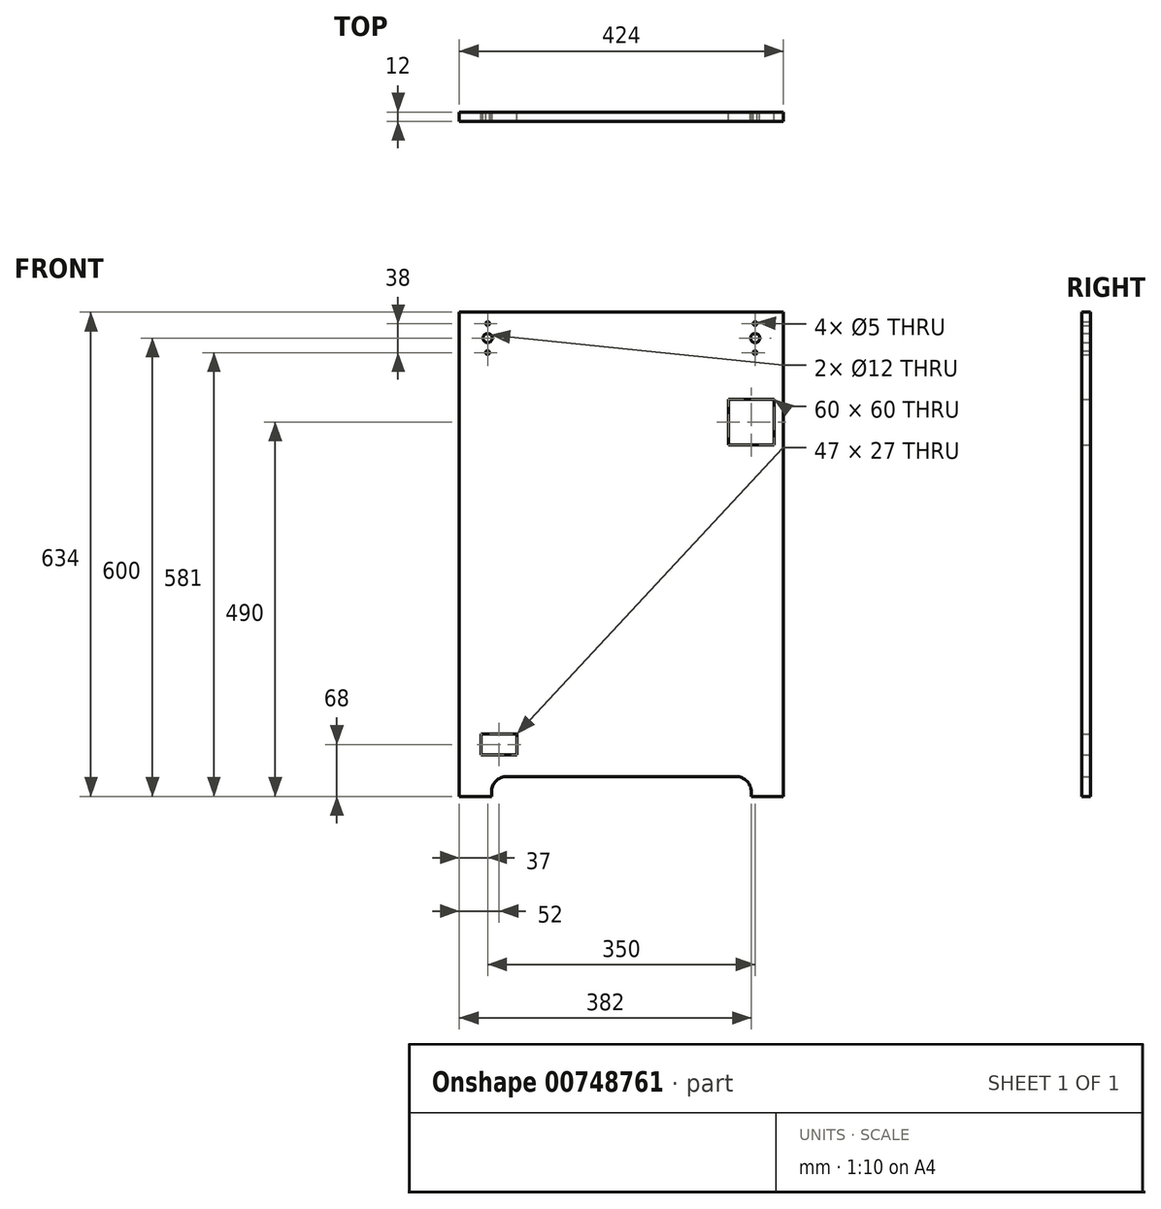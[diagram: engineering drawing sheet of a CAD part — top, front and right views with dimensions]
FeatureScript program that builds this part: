
annotation { "Feature Type Name" : "Feature", "Feature Type Description" : "" }
export const myFeature = defineFeature(function(context is Context, id is Id, definition is map)
    precondition{}
    {
        {
            assignVariable(context, id + "F0", {"name" : "Width", "anyValue" : 12});
        }
        {
            var Q0;
            Q0=qCreatedBy(makeId("Front.planeOp"),FACE);
            var sketch = newSketch(context, id + "F1", { "sketchPlane" : qUnion([Q0])});
            skLineSegment(sketch, "E0.bottom", {"start": v(200, 374) * mm, "end": v(-200, 374) * mm});
            skLineSegment(sketch, "E0.top", {"start": v(200, -260) * mm, "end": v(-200, -260) * mm});
            skLineSegment(sketch, "E0.left", {"start": v(200, 374) * mm, "end": v(200, -260) * mm});
            skLineSegment(sketch, "E0.right", {"start": v(-200, 374) * mm, "end": v(-200, -260) * mm});
            skPoint(sketch, "E1.middle", {"position": v(0, 0) * mm});
            skCircle(sketch, "E2", {"center": v(175, 340) * mm, "radius": 6 * mm});
            skCircle(sketch, "E3", {"center": v(-175, 340) * mm, "radius": 6 * mm});
            skLineSegment(sketch, "E4", {"start": v(200, -150) * mm, "end": v(-200, -150) * mm});
            skLineSegment(sketch, "E5", {"start": v(-200, -150) * mm, "end": v(-200, -162) * mm});
            skLineSegment(sketch, "E6", {"start": v(-200, -162) * mm, "end": v(200, -162) * mm});
            skLineSegment(sketch, "E7", {"start": v(200, -162) * mm, "end": v(200, -150) * mm});
            skLineSegment(sketch, "E8", {"start": v(-200, -260) * mm, "end": v(-212, -260) * mm});
            skLineSegment(sketch, "E9", {"start": v(-212, -260) * mm, "end": v(-212, 374) * mm});
            skLineSegment(sketch, "E10", {"start": v(-212, 374) * mm, "end": v(-200, 374) * mm});
            skLineSegment(sketch, "E11", {"start": v(200, 374) * mm, "end": v(212, 374) * mm});
            skLineSegment(sketch, "E12", {"start": v(212, 374) * mm, "end": v(212, -260) * mm});
            skLineSegment(sketch, "E13", {"start": v(212, -260) * mm, "end": v(200, -260) * mm});
            skLineSegment(sketch, "E14", {"start": v(-200, -222) * mm, "end": v(200, -222) * mm});
            skLineSegment(sketch, "E15", {"start": v(200, -222) * mm, "end": v(200, -234) * mm});
            skLineSegment(sketch, "E16", {"start": v(-200, -234) * mm, "end": v(-200, -222) * mm});
            skLineSegment(sketch, "E17", {"start": v(-170, -254) * mm, "end": v(-170, -260) * mm});
            skLineSegment(sketch, "E18", {"start": v(170, -254) * mm, "end": v(170, -260) * mm});
            skLineSegment(sketch, "E19", {"start": v(-150, -234) * mm, "end": v(150, -234) * mm});
            skArc(sketch, "E20.filletArc", {"start": v(170, -254) * mm, "mid": v(164.14, -239.86) * mm, "end": v(150, -234) * mm});
            skArc(sketch, "E21.filletArc", {"start": v(-150, -234) * mm, "mid": v(-164.14, -239.86) * mm, "end": v(-170, -254) * mm});
            skLineSegment(sketch, "E22", {"start": v(-200, -234) * mm, "end": v(-150, -234) * mm});
            skLineSegment(sketch, "E23", {"start": v(150, -234) * mm, "end": v(200, -234) * mm});
            skCircle(sketch, "E24", {"center": v(-175, 359) * mm, "radius": 2.5 * mm});
            skCircle(sketch, "E25", {"center": v(-175, 321) * mm, "radius": 2.5 * mm});
            skCircle(sketch, "E26", {"center": v(175, 359) * mm, "radius": 2.5 * mm});
            skCircle(sketch, "E27", {"center": v(175, 321) * mm, "radius": 2.5 * mm});
            skLineSegment(sketch, "E28.bottom", {"start": v(200, 200) * mm, "end": v(140, 200) * mm});
            skLineSegment(sketch, "E28.top", {"start": v(200, 260) * mm, "end": v(140, 260) * mm});
            skLineSegment(sketch, "E28.left", {"start": v(200, 200) * mm, "end": v(200, 260) * mm});
            skLineSegment(sketch, "E28.right", {"start": v(140, 200) * mm, "end": v(140, 260) * mm});
            skPoint(sketch, "E28.middle", {"position": v(170, 230) * mm});
            skLineSegment(sketch, "E29.bottom", {"start": v(-136.5, -178.5) * mm, "end": v(-183.5, -178.5) * mm});
            skLineSegment(sketch, "E29.top", {"start": v(-136.5, -205.5) * mm, "end": v(-183.5, -205.5) * mm});
            skLineSegment(sketch, "E29.left", {"start": v(-136.5, -178.5) * mm, "end": v(-136.5, -205.5) * mm});
            skLineSegment(sketch, "E29.right", {"start": v(-183.5, -178.5) * mm, "end": v(-183.5, -205.5) * mm});
            skSolve(sketch);
        }
        {
            var Q0;
            {var subQ1=sQuery(id+"F1.wireOp",EDGE,"E0.bottom");Q0=makeQuery(id+"F1.imprint","IMPRINT",FACE,{"disambiguationData":[TD([[makeQuery(id+"F1.imprint","IMPRINT",EDGE,{"derivedFrom":subQ1}),1.0]])]});}
            var Q1;
            {var subQ5=sQuery(id+"F1.wireOp",EDGE,"E11");Q1=makeQuery(id+"F1.imprint","IMPRINT",FACE,{"disambiguationData":[TD([[makeQuery(id+"F1.imprint","IMPRINT",EDGE,{"derivedFrom":subQ5}),-1.0]])]});}
            var Q2;
            {var subQ3=sQuery(id+"F1.wireOp",EDGE,"E8");Q2=makeQuery(id+"F1.imprint","IMPRINT",FACE,{"disambiguationData":[TD([[makeQuery(id+"F1.imprint","IMPRINT",EDGE,{"derivedFrom":subQ3}),-1.0]])]});}
            var Q3;
            {var subQ2=sQuery(id+"F1.wireOp",EDGE,"E4");Q3=makeQuery(id+"F1.imprint","IMPRINT",FACE,{"disambiguationData":[TD([[makeQuery(id+"F1.imprint","IMPRINT",EDGE,{"derivedFrom":subQ2}),1.0]])]});}
            var Q4;
            {var subQ1=sQuery(id+"F1.wireOp",EDGE,"E6");Q4=makeQuery(id+"F1.imprint","IMPRINT",FACE,{"disambiguationData":[TD([[makeQuery(id+"F1.imprint","IMPRINT",EDGE,{"derivedFrom":subQ1}),-1.0]])]});}
            var Q5;
            {var subQ0=sQuery(id+"F1.wireOp",EDGE,"E14");Q5=makeQuery(id+"F1.imprint","IMPRINT",FACE,{"disambiguationData":[TD([[makeQuery(id+"F1.imprint","IMPRINT",EDGE,{"derivedFrom":subQ0}),-1.0]])]});}
            var Q6;
            {var subQ0=sQuery(id+"F1.wireOp",EDGE,"E17");Q6=makeQuery(id+"F1.imprint","IMPRINT",FACE,{"disambiguationData":[TD([[makeQuery(id+"F1.imprint","IMPRINT",EDGE,{"derivedFrom":subQ0}),-1.0]])]});}
            var Q7;
            {var subQ4=sQuery(id+"F1.wireOp",EDGE,"E18");Q7=makeQuery(id+"F1.imprint","IMPRINT",FACE,{"disambiguationData":[TD([[makeQuery(id+"F1.imprint","IMPRINT",EDGE,{"derivedFrom":subQ4}),1.0]])]});}
            extrude(context, id + "F2", {"entities" : qUnion([Q0, Q1, Q2, Q3, Q4, Q5, Q6, Q7]), "depth" : (getVariable(context, 'Width')) * mm, "offsetDistance" : 25 * mm});
        }
    });
